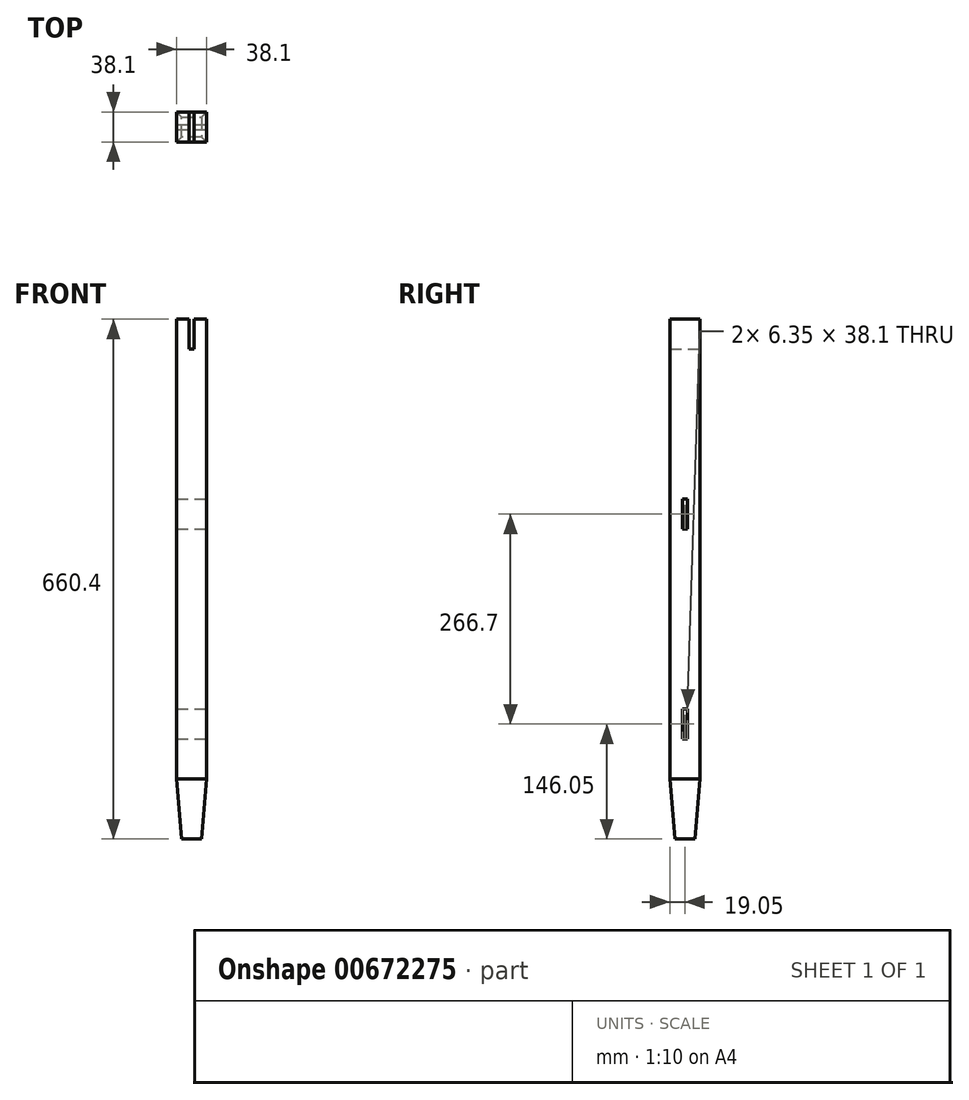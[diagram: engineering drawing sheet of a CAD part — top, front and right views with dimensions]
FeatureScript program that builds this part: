
annotation { "Feature Type Name" : "Feature", "Feature Type Description" : "" }
export const myFeature = defineFeature(function(context is Context, id is Id, definition is map)
    precondition{}
    {
        {
            var Q0;
            Q0=qCreatedBy(makeId("Front.planeOp"),FACE);
            var sketch = newSketch(context, id + "F0", { "sketchPlane" : qUnion([Q0])});
            skLineSegment(sketch, "E0.bottom", {"start": v(0, 0) * mm, "end": v(38.1, 0) * mm});
            skLineSegment(sketch, "E0.top", {"start": v(0, 660.4) * mm, "end": v(15.87, 660.4) * mm});
            skLineSegment(sketch, "E0.left", {"start": v(0, 0) * mm, "end": v(0, 660.4) * mm});
            skLineSegment(sketch, "E0.right", {"start": v(38.1, 0) * mm, "end": v(38.1, 660.4) * mm});
            skLineSegment(sketch, "E1.top", {"start": v(15.87, 622.3) * mm, "end": v(22.22, 622.3) * mm});
            skLineSegment(sketch, "E1.left", {"start": v(15.87, 660.4) * mm, "end": v(15.87, 622.3) * mm});
            skLineSegment(sketch, "E1.right", {"start": v(22.22, 660.4) * mm, "end": v(22.22, 622.3) * mm});
            skLineSegment(sketch, "E2.trimOffspring", {"start": v(22.22, 660.4) * mm, "end": v(38.1, 660.4) * mm});
            skSolve(sketch);
        }
        {
            var Q0;
            Q0=makeQuery(id+"F0.imprint","IMPRINT",FACE,{"disambiguationData":[TD([[makeQuery(id+"F0.imprint","IMPRINT",EDGE,{"derivedFrom":sQuery(id+"F0.wireOp",EDGE,"E0.bottom")}),1.0]])]});
            extrude(context, id + "F1", {"entities" : qUnion([Q0]), "depth" : 38.1 * mm, "offsetDistance" : 25.4 * mm});
        }
        {
            var Q0;
            Q0=makeQuery(id+"F1.opExtrude","CAP_EDGE",EDGE,{"disambiguationData":[OSD([sQuery(id+"F0.wireOp",EDGE,"E0.bottom")])],"isStart":false});
            var Q1;
            Q1=makeQuery(id+"F1.opExtrude","SWEPT_EDGE",EDGE,{"disambiguationData":[OSD([sQuery(id+"F0.wireOp",EDGE,"E0.bottom"),sQuery(id+"F0.wireOp",EDGE,"E0.right")])]});
            var Q2;
            Q2=makeQuery(id+"F1.opExtrude","CAP_EDGE",EDGE,{"disambiguationData":[OSD([sQuery(id+"F0.wireOp",EDGE,"E0.bottom")])],"isStart":true});
            var Q3;
            Q3=makeQuery(id+"F1.opExtrude","SWEPT_EDGE",EDGE,{"disambiguationData":[OSD([sQuery(id+"F0.wireOp",EDGE,"E0.bottom"),sQuery(id+"F0.wireOp",EDGE,"E0.left")])]});
            chamfer(context, id + "F2", {"entities" : qUnion([Q0, Q1, Q2, Q3]), "chamferType" : ChamferType.TWO_OFFSETS, "width1" : 76.2 * mm, "oppositeDirection" : false, "width2" : 6.35 * mm, "tangentPropagation" : true});
        }
        {
            var Q0;
            Q0=makeQuery(id+"F1.opExtrude","SWEPT_FACE",FACE,{"disambiguationData":[OSD([sQuery(id+"F0.wireOp",EDGE,"E0.right")])]});
            var sketch = newSketch(context, id + "F3", { "sketchPlane" : qUnion([Q0])});
            skLineSegment(sketch, "E3.bottom", {"start": v(-22.22, 393.7) * mm, "end": v(-15.87, 393.7) * mm});
            skLineSegment(sketch, "E3.top", {"start": v(-22.23, 431.8) * mm, "end": v(-15.88, 431.8) * mm});
            skLineSegment(sketch, "E3.left", {"start": v(-22.22, 393.7) * mm, "end": v(-22.23, 431.8) * mm});
            skLineSegment(sketch, "E3.right", {"start": v(-15.87, 393.7) * mm, "end": v(-15.88, 431.8) * mm});
            skLineSegment(sketch, "E4.bottom", {"start": v(-22.22, 127) * mm, "end": v(-15.87, 127) * mm});
            skLineSegment(sketch, "E4.top", {"start": v(-22.22, 165.1) * mm, "end": v(-15.87, 165.1) * mm});
            skLineSegment(sketch, "E4.left", {"start": v(-22.22, 127) * mm, "end": v(-22.22, 165.1) * mm});
            skLineSegment(sketch, "E4.right", {"start": v(-15.88, 127) * mm, "end": v(-15.88, 165.1) * mm});
            skSolve(sketch);
        }
        {
            var Q0;
            Q0=makeQuery(id+"F3.imprint","IMPRINT",FACE,{"disambiguationData":[TD([[makeQuery(id+"F3.imprint","IMPRINT",EDGE,{"derivedFrom":sQuery(id+"F3.wireOp",EDGE,"E3.bottom")}),1.0]])]});
            var Q1;
            Q1=makeQuery(id+"F3.imprint","IMPRINT",FACE,{"disambiguationData":[TD([[makeQuery(id+"F3.imprint","IMPRINT",EDGE,{"derivedFrom":sQuery(id+"F3.wireOp",EDGE,"E4.bottom")}),1.0]])]});
            extrude(context, id + "F4", {"entities" : qUnion([Q0, Q1]), "operationType" : NewBodyOperationType.REMOVE, "endBound" : BoundingType.THROUGH_ALL, "oppositeDirection" : true, "depth" : 25.4 * mm, "offsetDistance" : 25.4 * mm});
        }
    });
